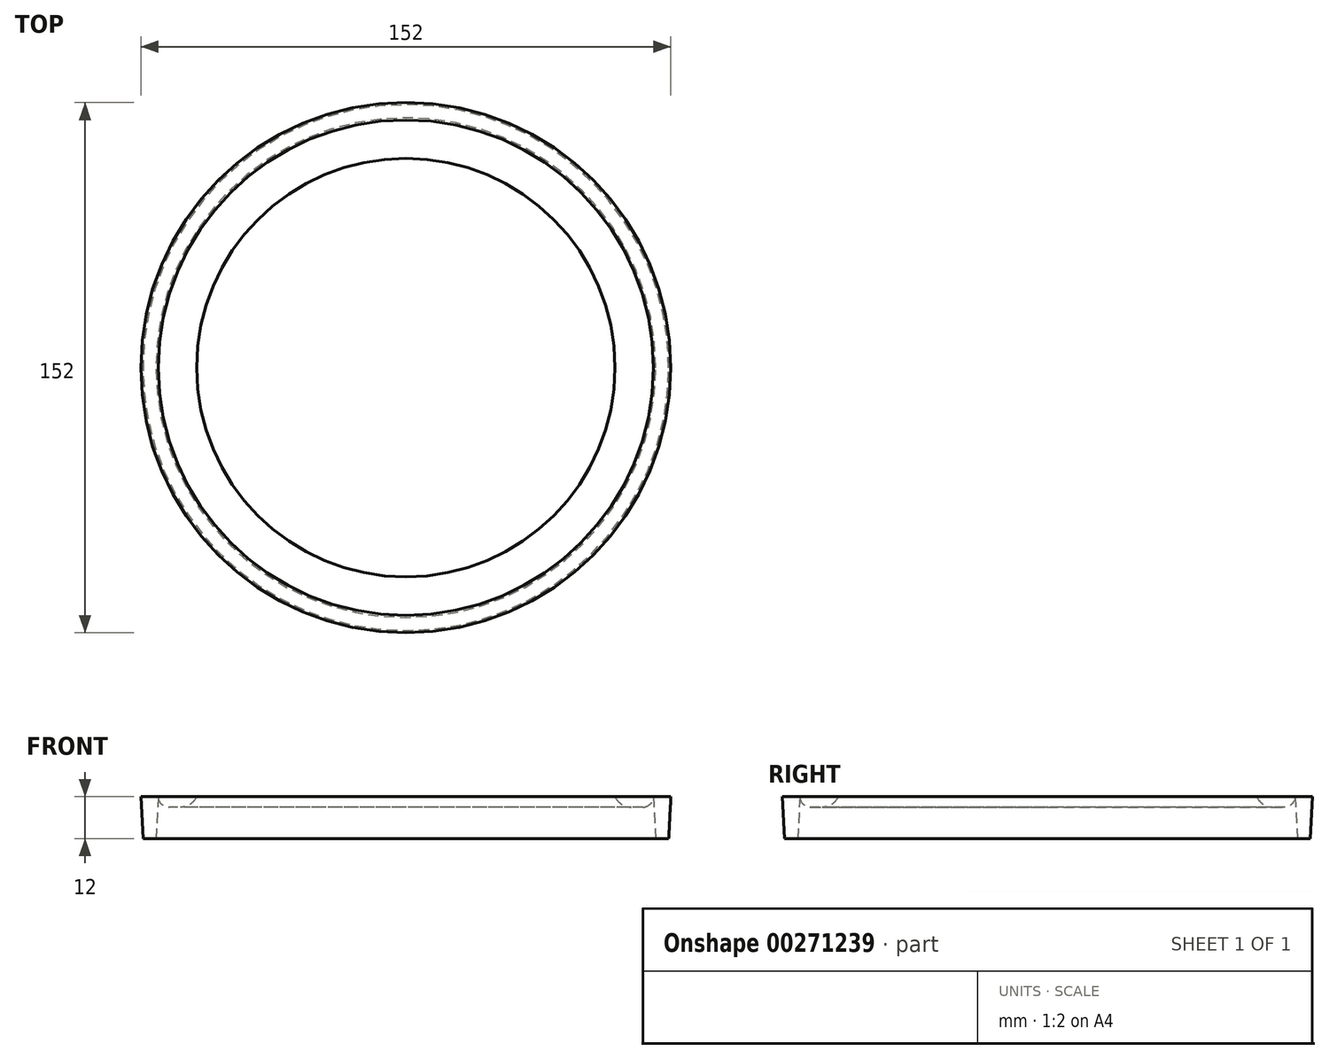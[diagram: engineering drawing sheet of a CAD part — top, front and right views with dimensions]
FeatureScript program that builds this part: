
annotation { "Feature Type Name" : "Feature", "Feature Type Description" : "" }
export const myFeature = defineFeature(function(context is Context, id is Id, definition is map)
    precondition{}
    {
        {
            var Q0;
            Q0=qCreatedBy(makeId("Top.planeOp"),FACE);
            var sketch = newSketch(context, id + "F0", { "sketchPlane" : qUnion([Q0])});
            skCircle(sketch, "E0", {"center": v(0, 0) * mm, "radius": 76 * mm});
            skCircle(sketch, "E1", {"center": v(0, 0) * mm, "radius": 71 * mm});
            skCircle(sketch, "E2", {"center": v(0, 0) * mm, "radius": 65 * mm});
            skCircle(sketch, "E3", {"center": v(0, 0) * mm, "radius": 60 * mm});
            skSolve(sketch);
        }
        {
            var Q0;
            Q0=makeQuery(id+"F0.imprint","IMPRINT",FACE,{"disambiguationData":[TD([[makeQuery(id+"F0.imprint","IMPRINT",EDGE,{"derivedFrom":sQuery(id+"F0.wireOp",EDGE,"E0")}),1.0]])]});
            extrude(context, id + "F1", {"entities" : qUnion([Q0]), "oppositeDirection" : true, "depth" : 12 * mm, "hasDraft" : true, "draftAngle" : 3 * degree, "draftPullDirection" : true});
        }
        {
            var Q0;
            Q0=makeQuery(id+"F0.imprint","IMPRINT",FACE,{"disambiguationData":[TD([[makeQuery(id+"F0.imprint","IMPRINT",EDGE,{"derivedFrom":sQuery(id+"F0.wireOp",EDGE,"E1")}),1.0]])]});
            var Q1;
            Q1=makeQuery(id+"F0.imprint","IMPRINT",FACE,{"disambiguationData":[TD([[makeQuery(id+"F0.imprint","IMPRINT",EDGE,{"derivedFrom":sQuery(id+"F0.wireOp",EDGE,"E2")}),1.0]])]});
            extrude(context, id + "F2", {"entities" : qUnion([Q0, Q1]), "operationType" : NewBodyOperationType.ADD, "oppositeDirection" : true, "depth" : 3 * mm});
        }
        {
            var Q0;
            Q0=qCreatedBy(makeId("Right.planeOp"),FACE);
            var sketch = newSketch(context, id + "F3", { "sketchPlane" : qUnion([Q0])});
            skLineSegment(sketch, "E4.0", {"start": v(-65, 0) * mm, "end": v(-60, 0) * mm});
            skArc(sketch, "E5", {"start": v(60, 0) * mm, "mid": v(0, 60) * mm, "end": v(-60, 0) * mm});
            skArc(sketch, "E6", {"start": v(65, 0) * mm, "mid": v(0, 65) * mm, "end": v(-65, 0) * mm});
            skLineSegment(sketch, "E7", {"start": v(65, 0) * mm, "end": v(60, 0) * mm});
            skLineSegment(sketch, "E8", {"start": v(-60, 0) * mm, "end": v(-65, 0) * mm});
            skLineSegment(sketch, "E9.trimOffspring", {"start": v(60, 0) * mm, "end": v(65, 0) * mm});
            skSolve(sketch);
        }
        {
            var Q0;
            Q0=qCreatedBy(makeId("Front.planeOp"),FACE);
            var sketch = newSketch(context, id + "F4", { "sketchPlane" : qUnion([Q0])});
            skLineSegment(sketch, "E10.0", {"start": v(-65, 0) * mm, "end": v(-60, 0) * mm});
            skArc(sketch, "E11", {"start": v(60, 0) * mm, "mid": v(0, 60) * mm, "end": v(-60, 0) * mm});
            skArc(sketch, "E12", {"start": v(65, 0) * mm, "mid": v(0, 65) * mm, "end": v(-65, 0) * mm});
            skLineSegment(sketch, "E13", {"start": v(65, 0) * mm, "end": v(60, 0) * mm});
            skLineSegment(sketch, "E14", {"start": v(-60, 0) * mm, "end": v(-65, 0) * mm});
            skLineSegment(sketch, "E15.trimOffspring", {"start": v(60, 0) * mm, "end": v(65, 0) * mm});
            skSolve(sketch);
        }
        {
            var Q0;
            Q0=makeQuery(id+"F2.opExtrude","CAP_EDGE",EDGE,{"disambiguationData":[OSD([sQuery(id+"F0.wireOp",EDGE,"E3")])],"isStart":false});
            fillet(context, id + "F5", {"entities" : qUnion([Q0]), "radius" : 5 * mm, "tangentPropagation" : true, "allowEdgeOverflow" : false});
        }
        {
            var Q0;
            Q0=makeQuery(id+"F2.opExtrude","CAP_EDGE",EDGE,{"disambiguationData":[OSD([sQuery(id+"F0.wireOp",EDGE,"E1")])],"isStart":false});
            fillet(context, id + "F6", {"entities" : qUnion([Q0]), "radius" : 3 * mm, "tangentPropagation" : true, "allowEdgeOverflow" : false});
        }
    });
